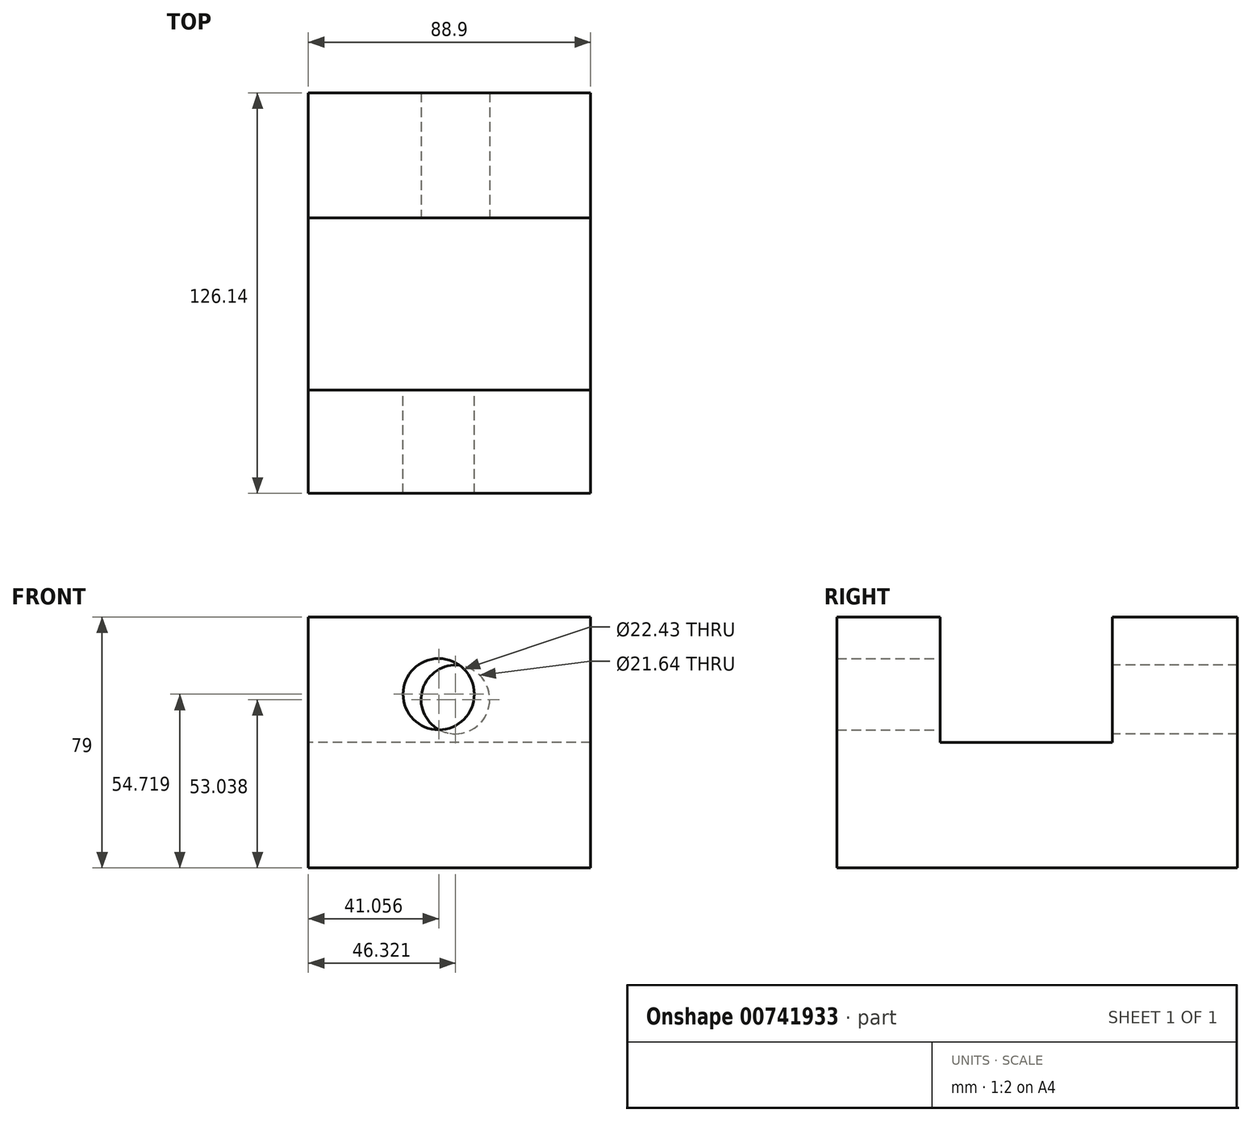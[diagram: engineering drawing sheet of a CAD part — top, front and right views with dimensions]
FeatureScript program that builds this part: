
annotation { "Feature Type Name" : "Feature", "Feature Type Description" : "" }
export const myFeature = defineFeature(function(context is Context, id is Id, definition is map)
    precondition{}
    {
        {
            var Q0;
            Q0=qCreatedBy(makeId("Right.planeOp"),FACE);
            var sketch = newSketch(context, id + "F0", { "sketchPlane" : qUnion([Q0])});
            skLineSegment(sketch, "E0.bottom", {"start": v(63.07, 39.5) * mm, "end": v(23.72, 39.5) * mm});
            skLineSegment(sketch, "E0.top", {"start": v(63.07, -39.5) * mm, "end": v(-63.07, -39.5) * mm});
            skLineSegment(sketch, "E0.left", {"start": v(63.07, 39.5) * mm, "end": v(63.07, -39.5) * mm});
            skLineSegment(sketch, "E0.right", {"start": v(-63.07, 39.5) * mm, "end": v(-63.07, -39.5) * mm});
            skPoint(sketch, "E0.middle", {"position": v(0, 0) * mm});
            skLineSegment(sketch, "E1", {"start": v(-30.52, 39.5) * mm, "end": v(-30.52, 0) * mm});
            skLineSegment(sketch, "E2", {"start": v(-30.52, 0) * mm, "end": v(23.72, 0) * mm});
            skLineSegment(sketch, "E3", {"start": v(23.72, 0) * mm, "end": v(23.72, 39.5) * mm});
            skLineSegment(sketch, "E4.trimOffspring", {"start": v(-30.52, 39.5) * mm, "end": v(-63.07, 39.5) * mm});
            skSolve(sketch);
        }
        {
            var Q0;
            Q0=makeQuery(id+"F0.imprint","IMPRINT",FACE,{"disambiguationData":[TD([[makeQuery(id+"F0.imprint","IMPRINT",EDGE,{"derivedFrom":sQuery(id+"F0.wireOp",EDGE,"E0.bottom")}),1.0]])]});
            extrude(context, id + "F1", {"entities" : qUnion([Q0]), "depth" : 88.9 * mm, "offsetDistance" : 25.4 * mm});
        }
        {
            var Q0;
            Q0=qCreatedBy(makeId("Front.planeOp"),FACE);
            var sketch = newSketch(context, id + "F2", { "sketchPlane" : qUnion([Q0])});
            skCircle(sketch, "E5", {"center": v(41.06, 15.22) * mm, "radius": 11.21 * mm});
            skSolve(sketch);
        }
        {
            var Q0;
            Q0 = qSketchRegion(id + "F2", true);
            extrude(context, id + "F3", {"entities" : qUnion([Q0]), "operationType" : NewBodyOperationType.REMOVE, "depth" : 76.2 * mm, "offsetDistance" : 25.4 * mm});
        }
        {
            var Q0;
            Q0=qCreatedBy(makeId("Front.planeOp"),FACE);
            var sketch = newSketch(context, id + "F4", { "sketchPlane" : qUnion([Q0])});
            skCircle(sketch, "E6", {"center": v(46.32, 13.54) * mm, "radius": 10.82 * mm});
            skSolve(sketch);
        }
        {
            var Q0;
            Q0 = qSketchRegion(id + "F4", true);
            extrude(context, id + "F5", {"entities" : qUnion([Q0]), "operationType" : NewBodyOperationType.REMOVE, "oppositeDirection" : true, "depth" : 76.2 * mm, "offsetDistance" : 25.4 * mm});
        }
    });
